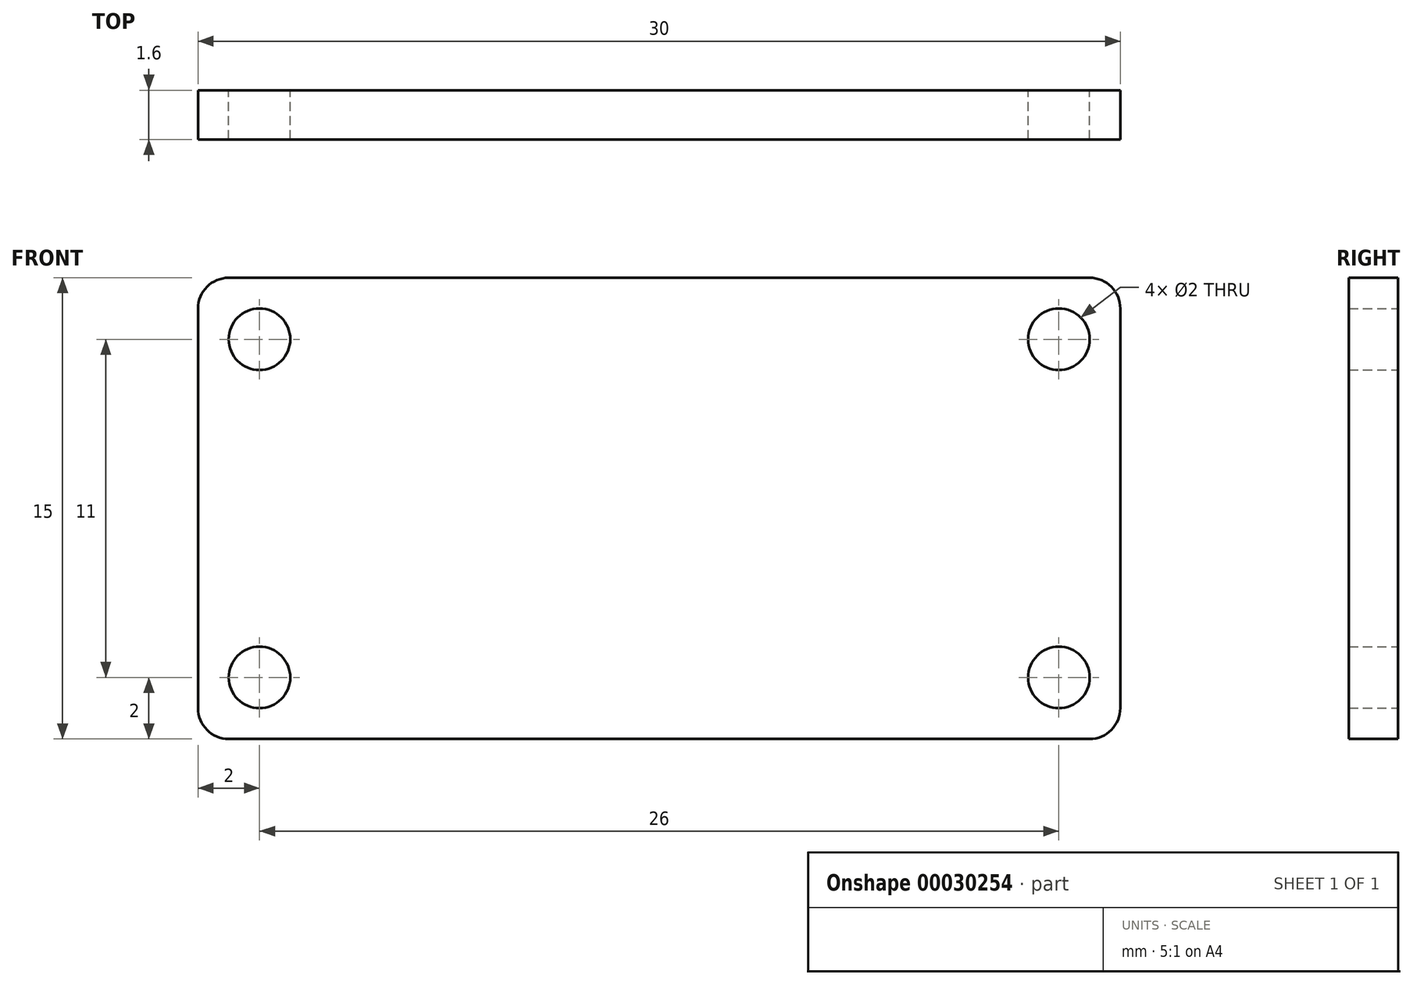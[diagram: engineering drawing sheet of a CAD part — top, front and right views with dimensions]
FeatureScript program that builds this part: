
annotation { "Feature Type Name" : "Feature", "Feature Type Description" : "" }
export const myFeature = defineFeature(function(context is Context, id is Id, definition is map)
    precondition{}
    {
        {
            var Q0;
            Q0=qCreatedBy(makeId("Front.planeOp"),FACE);
            var sketch = newSketch(context, id + "F0", { "sketchPlane" : qUnion([Q0])});
            skLineSegment(sketch, "E0.bottom", {"start": v(14, -7.5) * mm, "end": v(-14, -7.5) * mm});
            skLineSegment(sketch, "E0.top", {"start": v(14, 7.5) * mm, "end": v(-14, 7.5) * mm});
            skLineSegment(sketch, "E0.left", {"start": v(15, -6.5) * mm, "end": v(15, 6.5) * mm});
            skLineSegment(sketch, "E0.right", {"start": v(-15, -6.5) * mm, "end": v(-15, 6.5) * mm});
            skPoint(sketch, "E0.middle", {"position": v(0, 0) * mm});
            skPoint(sketch, "E1.visualSharp", {"position": v(-15, 7.5) * mm});
            skArc(sketch, "E1.filletArc", {"start": v(-14, 7.5) * mm, "mid": v(-14.7, 7.2) * mm, "end": v(-15, 6.5) * mm});
            skPoint(sketch, "E2.visualSharp", {"position": v(15, 7.5) * mm});
            skArc(sketch, "E2.filletArc", {"start": v(15, 6.5) * mm, "mid": v(14.7, 7.2) * mm, "end": v(14, 7.5) * mm});
            skPoint(sketch, "E3.visualSharp", {"position": v(15, -7.5) * mm});
            skArc(sketch, "E3.filletArc", {"start": v(14, -7.5) * mm, "mid": v(14.7, -7.2) * mm, "end": v(15, -6.5) * mm});
            skPoint(sketch, "E4.visualSharp", {"position": v(-15, -7.5) * mm});
            skArc(sketch, "E4.filletArc", {"start": v(-15, -6.5) * mm, "mid": v(-14.7, -7.2) * mm, "end": v(-14, -7.5) * mm});
            skPoint(sketch, "E5", {"position": v(-13, 5.5) * mm});
            skPoint(sketch, "E6.MirrorP", {"position": v(-13, -5.5) * mm});
            skPoint(sketch, "E7.MirrorP", {"position": v(13, 5.5) * mm});
            skPoint(sketch, "E8.MirrorP", {"position": v(13, -5.5) * mm});
            skSolve(sketch);
        }
        {
            var Q0;
            Q0=makeQuery(id+"F0.imprint","IMPRINT",FACE,{"disambiguationData":[TD([[makeQuery(id+"F0.imprint","IMPRINT",EDGE,{"derivedFrom":sQuery(id+"F0.wireOp",EDGE,"E0.bottom")}),-1.0]])]});
            extrude(context, id + "F1", {"entities" : qUnion([Q0]), "depth" : 1.6 * mm});
        }
        {
            var Q0;
            Q0=sQuery(id+"F0.wireOp",VERTEX,"E5");
            var Q1;
            Q1=sQuery(id+"F0.wireOp",VERTEX,"E6.MirrorP");
            var Q2;
            Q2=sQuery(id+"F0.wireOp",VERTEX,"E8.MirrorP");
            var Q3;
            Q3=sQuery(id+"F0.wireOp",VERTEX,"E7.MirrorP");
            var Q4;
            Q4=makeQuery(id+"F1.opExtrude","SWEPT_BODY",BODY,{"disambiguationData":[OSD([sQuery(id+"F0.wireOp",EDGE,"E0.bottom"),sQuery(id+"F0.wireOp",EDGE,"E0.top"),sQuery(id+"F0.wireOp",EDGE,"E0.left"),sQuery(id+"F0.wireOp",EDGE,"E0.right"),sQuery(id+"F0.wireOp",EDGE,"E1.filletArc"),sQuery(id+"F0.wireOp",EDGE,"E2.filletArc"),sQuery(id+"F0.wireOp",EDGE,"E3.filletArc"),sQuery(id+"F0.wireOp",EDGE,"E4.filletArc")])]});
            hole(context, id + "F2", {"style" : HoleStyle.SIMPLE, "holeDiameter" : 2 * mm, "endStyle" : HoleEndStyle.THROUGH, "oppositeDirection" : true, "locations" : qUnion([Q0, Q1, Q2, Q3]), "scope" : qUnion([Q4])});
        }
    });
